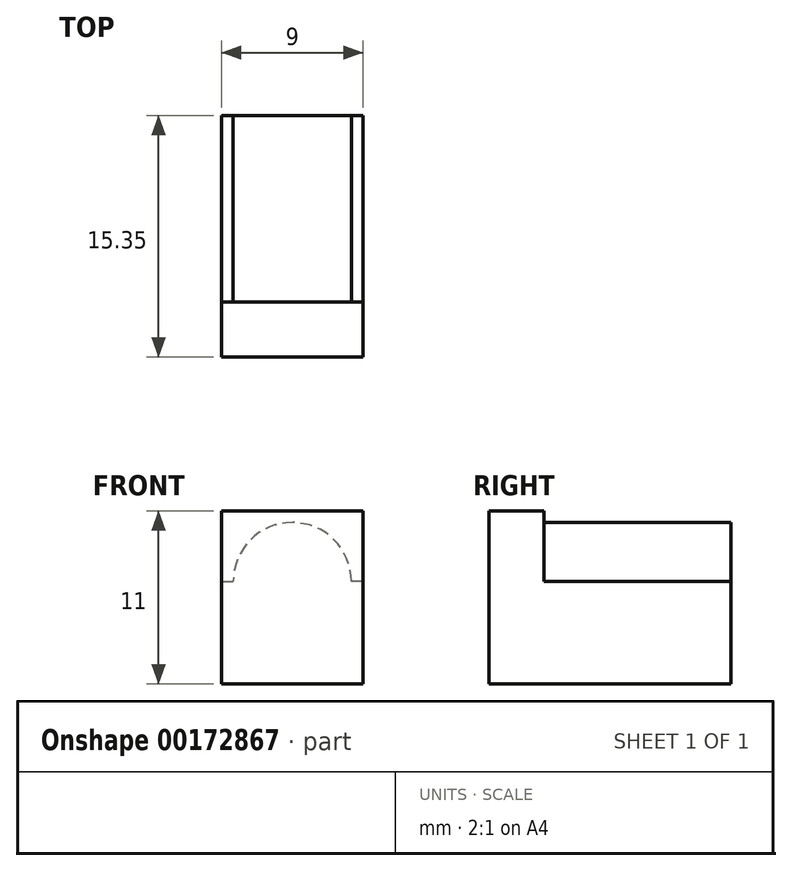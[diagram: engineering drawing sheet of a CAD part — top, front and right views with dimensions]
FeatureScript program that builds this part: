
annotation { "Feature Type Name" : "Feature", "Feature Type Description" : "" }
export const myFeature = defineFeature(function(context is Context, id is Id, definition is map)
    precondition{}
    {
        {
            var Q0;
            Q0=qCreatedBy(makeId("Front.planeOp"),FACE);
            var sketch = newSketch(context, id + "F0", { "sketchPlane" : qUnion([Q0])});
            skLineSegment(sketch, "E0.bottom", {"start": v(4.5, 0) * mm, "end": v(-4.5, 0) * mm});
            skLineSegment(sketch, "E0.top", {"start": v(4.5, 11) * mm, "end": v(-4.5, 11) * mm});
            skLineSegment(sketch, "E0.left", {"start": v(4.5, 0) * mm, "end": v(4.5, 11) * mm});
            skLineSegment(sketch, "E0.right", {"start": v(-4.5, 0) * mm, "end": v(-4.5, 11) * mm});
            skPoint(sketch, "E0.middle", {"position": v(0, 5.5) * mm});
            skSolve(sketch);
        }
        {
            var Q0;
            Q0 = qSketchRegion(id + "F0", true);
            extrude(context, id + "F1", {"entities" : qUnion([Q0]), "oppositeDirection" : true, "depth" : 3.5 * mm});
        }
        {
            var Q0;
            Q0=makeQuery(id+"F1.opExtrude","CAP_FACE",FACE,{"disambiguationData":[OSD([sQuery(id+"F0.wireOp",EDGE,"E0.bottom"),sQuery(id+"F0.wireOp",EDGE,"E0.top"),sQuery(id+"F0.wireOp",EDGE,"E0.left"),sQuery(id+"F0.wireOp",EDGE,"E0.right")])],"isStart":false});
            var sketch = newSketch(context, id + "F2", { "sketchPlane" : qUnion([Q0])});
            skLineSegment(sketch, "E1.1", {"start": v(-4.5, 0) * mm, "end": v(4.5, 0) * mm});
            skArc(sketch, "E2", {"start": v(3.75, 6.5) * mm, "mid": v(0, 10.25) * mm, "end": v(-3.75, 6.5) * mm});
            skLineSegment(sketch, "E3", {"start": v(-4.5, 0) * mm, "end": v(-4.5, 6.5) * mm});
            skLineSegment(sketch, "E4", {"start": v(-4.5, 6.5) * mm, "end": v(-3.75, 6.5) * mm});
            skLineSegment(sketch, "E5.MirrorCS", {"start": v(4.5, 6.5) * mm, "end": v(3.75, 6.5) * mm});
            skLineSegment(sketch, "E6.MirrorCS", {"start": v(4.5, 0) * mm, "end": v(4.5, 6.5) * mm});
            skSolve(sketch);
        }
        {
            var Q0;
            Q0 = qSketchRegion(id + "F2", true);
            extrude(context, id + "F3", {"entities" : qUnion([Q0]), "operationType" : NewBodyOperationType.ADD, "depth" : 11.85 * mm});
        }
    });
